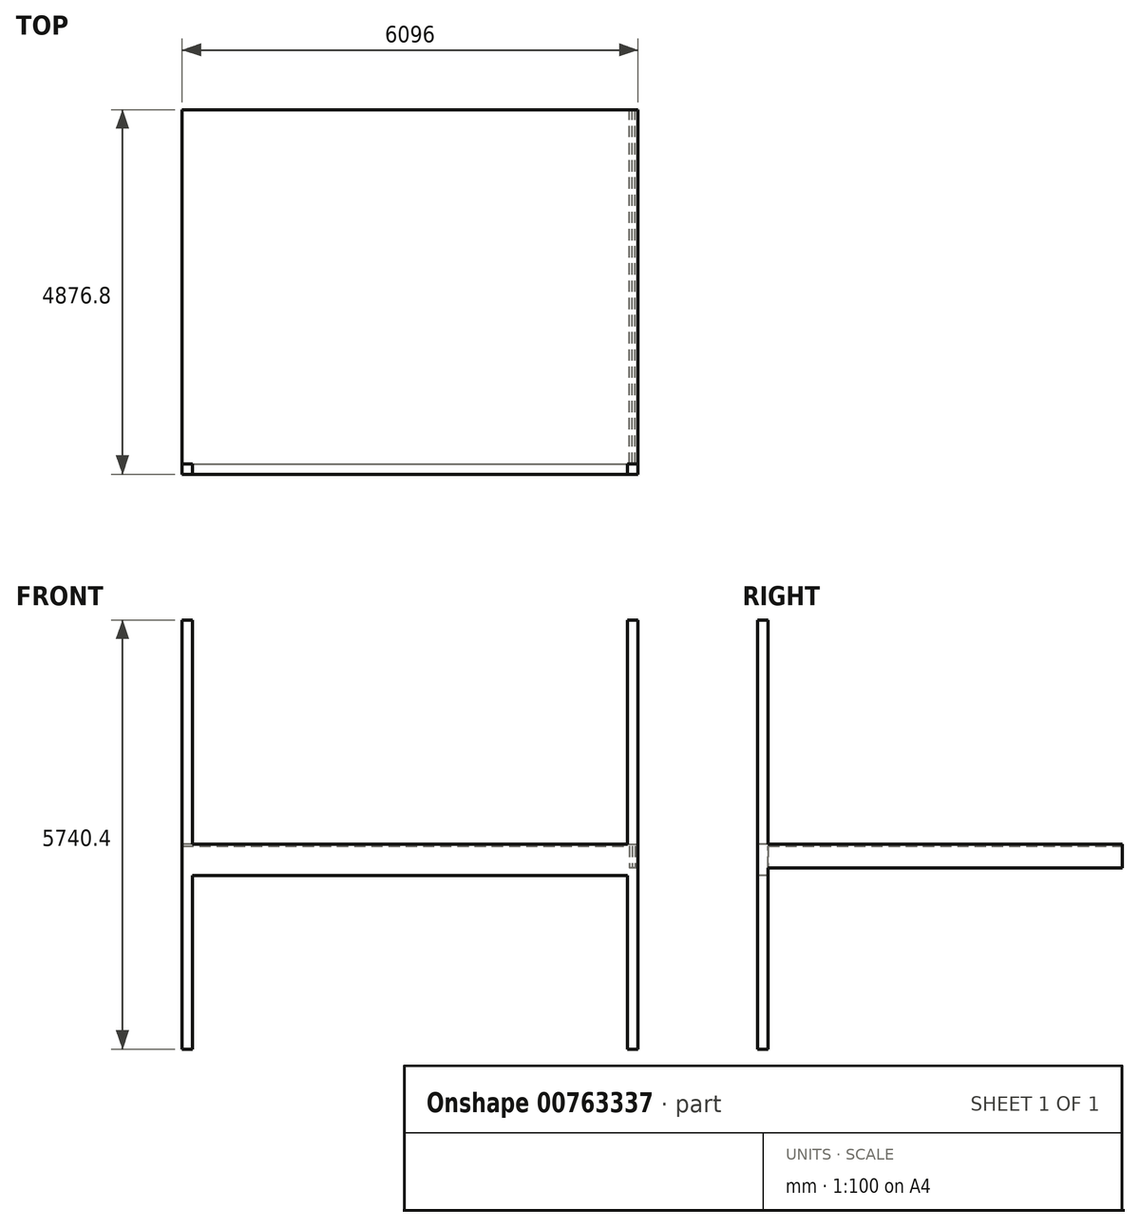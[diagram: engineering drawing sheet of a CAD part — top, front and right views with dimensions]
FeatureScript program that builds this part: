
annotation { "Feature Type Name" : "Feature", "Feature Type Description" : "" }
export const myFeature = defineFeature(function(context is Context, id is Id, definition is map)
    precondition{}
    {
        {
            var Q0;
            Q0=qCreatedBy(makeId("Right.planeOp"),FACE);
            var sketch = newSketch(context, id + "F0", { "sketchPlane" : qUnion([Q0])});
            skLineSegment(sketch, "E0.bottom", {"start": v(0, 2971.8) * mm, "end": v(-4876.8, 2971.8) * mm});
            skLineSegment(sketch, "E0.top", {"start": v(0, 2997.2) * mm, "end": v(-4876.8, 2997.2) * mm});
            skLineSegment(sketch, "E0.left", {"start": v(0, 2971.8) * mm, "end": v(0, 2997.2) * mm});
            skLineSegment(sketch, "E0.right", {"start": v(-4876.8, 2971.8) * mm, "end": v(-4876.8, 2997.2) * mm});
            skLineSegment(sketch, "E1", {"start": v(0, 0) * mm, "end": v(0, 6096) * mm, "construction": true});
            skSolve(sketch);
        }
        {
            var Q0;
            Q0=makeQuery(id+"F0.imprint","IMPRINT",FACE,{"disambiguationData":[TD([[makeQuery(id+"F0.imprint","IMPRINT",EDGE,{"derivedFrom":sQuery(id+"F0.wireOp",EDGE,"E0.bottom")}),-1.0]])]});
            extrude(context, id + "F1", {"entities" : qUnion([Q0]), "oppositeDirection" : true, "depth" : 6096 * mm, "offsetDistance" : 25.4 * mm});
        }
        {
            var Q0;
            Q0=makeQuery(id+"F1.opExtrude","SWEPT_FACE",FACE,{"disambiguationData":[OSD([sQuery(id+"F0.wireOp",EDGE,"E0.top")])]});
            var sketch = newSketch(context, id + "F2", { "sketchPlane" : qUnion([Q0])});
            skLineSegment(sketch, "E2.bottom", {"start": v(0, -4876.8) * mm, "end": v(-139.7, -4876.8) * mm});
            skLineSegment(sketch, "E2.top", {"start": v(0, -4737.1) * mm, "end": v(-139.7, -4737.1) * mm});
            skLineSegment(sketch, "E2.left", {"start": v(0, -4876.8) * mm, "end": v(0, -4737.1) * mm});
            skLineSegment(sketch, "E2.right", {"start": v(-139.7, -4876.8) * mm, "end": v(-139.7, -4737.1) * mm});
            skLineSegment(sketch, "E3.bottom", {"start": v(-6096, -4876.8) * mm, "end": v(-5956.3, -4876.8) * mm});
            skLineSegment(sketch, "E3.top", {"start": v(-6096, -4737.1) * mm, "end": v(-5956.3, -4737.1) * mm});
            skLineSegment(sketch, "E3.left", {"start": v(-6096, -4876.8) * mm, "end": v(-6096, -4737.1) * mm});
            skLineSegment(sketch, "E3.right", {"start": v(-5956.3, -4876.8) * mm, "end": v(-5956.3, -4737.1) * mm});
            skSolve(sketch);
        }
        {
            var Q0;
            Q0 = qSketchRegion(id + "F2", true);
            extrude(context, id + "F3", {"entities" : qUnion([Q0]), "operationType" : NewBodyOperationType.ADD, "depth" : 2997.2 * mm, "offsetDistance" : 25.4 * mm, "hasSecondDirection" : true, "secondDirectionOppositeDirection" : true, "secondDirectionDepth" : 2743.2 * mm});
        }
        {
            var Q0;
            Q0=makeQuery(id+"F3.boolean.opBoolean","MERGE",FACE,{"derivedFrom":[makeQuery(id+"F1.opExtrude","CAP_FACE",FACE,{"disambiguationData":[OSD([sQuery(id+"F0.wireOp",EDGE,"E0.bottom"),sQuery(id+"F0.wireOp",EDGE,"E0.top"),sQuery(id+"F0.wireOp",EDGE,"E0.left"),sQuery(id+"F0.wireOp",EDGE,"E0.right")])],"isStart":true}),makeQuery(id+"F3.opExtrude","SWEPT_FACE",FACE,{"disambiguationData":[OSD([sQuery(id+"F2.wireOp",EDGE,"E2.left")])]})]});
            var sketch = newSketch(context, id + "F4", { "sketchPlane" : qUnion([Q0])});
            skLineSegment(sketch, "E4.bottom", {"start": v(-4876.8, 2971.8) * mm, "end": v(-4737.1, 2971.8) * mm});
            skLineSegment(sketch, "E4.top", {"start": v(-4876.8, 2578.1) * mm, "end": v(-4737.1, 2578.1) * mm});
            skLineSegment(sketch, "E4.left", {"start": v(-4876.8, 2971.8) * mm, "end": v(-4876.8, 2578.1) * mm});
            skLineSegment(sketch, "E4.right", {"start": v(-4737.1, 2971.8) * mm, "end": v(-4737.1, 2578.1) * mm});
            skSolve(sketch);
        }
        {
            var Q0;
            Q0 = qSketchRegion(id + "F4", true);
            extrude(context, id + "F5", {"entities" : qUnion([Q0]), "operationType" : NewBodyOperationType.ADD, "oppositeDirection" : true, "depth" : 6096 * mm, "offsetDistance" : 25.4 * mm});
        }
        {
            var Q0;
            Q0=makeQuery(id+"F1.opExtrude","SWEPT_FACE",FACE,{"disambiguationData":[OSD([sQuery(id+"F0.wireOp",EDGE,"E0.left")])]});
            var sketch = newSketch(context, id + "F6", { "sketchPlane" : qUnion([Q0])});
            skLineSegment(sketch, "E5.bottom", {"start": v(0, 2971.8) * mm, "end": v(38.1, 2971.8) * mm});
            skLineSegment(sketch, "E5.top", {"start": v(0, 2679.7) * mm, "end": v(38.1, 2679.7) * mm});
            skLineSegment(sketch, "E5.left", {"start": v(0, 2971.8) * mm, "end": v(0, 2679.7) * mm});
            skLineSegment(sketch, "E5.right", {"start": v(38.1, 2971.8) * mm, "end": v(38.1, 2679.7) * mm});
            skLineSegment(sketch, "E6.bottom", {"start": v(38.23, 2971.8) * mm, "end": v(76.33, 2971.8) * mm});
            skLineSegment(sketch, "E6.top", {"start": v(38.23, 2679.7) * mm, "end": v(76.33, 2679.7) * mm});
            skLineSegment(sketch, "E6.left", {"start": v(38.23, 2971.8) * mm, "end": v(38.23, 2679.7) * mm});
            skLineSegment(sketch, "E6.right", {"start": v(76.33, 2971.8) * mm, "end": v(76.33, 2679.7) * mm});
            skLineSegment(sketch, "E7.bottom", {"start": v(76.45, 2971.8) * mm, "end": v(114.55, 2971.8) * mm});
            skLineSegment(sketch, "E7.top", {"start": v(76.45, 2679.7) * mm, "end": v(114.55, 2679.7) * mm});
            skLineSegment(sketch, "E7.left", {"start": v(76.45, 2971.8) * mm, "end": v(76.45, 2679.7) * mm});
            skLineSegment(sketch, "E7.right", {"start": v(114.55, 2971.8) * mm, "end": v(114.55, 2679.7) * mm});
            skLineSegment(sketch, "E8", {"start": v(38.1, 2971.8) * mm, "end": v(38.23, 2971.8) * mm, "construction": true});
            skLineSegment(sketch, "E9", {"start": v(76.33, 2971.8) * mm, "end": v(76.45, 2971.8) * mm, "construction": true});
            skSolve(sketch);
        }
        {
            var Q0;
            Q0 = qSketchRegion(id + "F6", true);
            extrude(context, id + "F7", {"entities" : qUnion([Q0]), "operationType" : NewBodyOperationType.ADD, "oppositeDirection" : true, "depth" : 4876.8 * mm, "offsetDistance" : 25.4 * mm});
        }
    });
